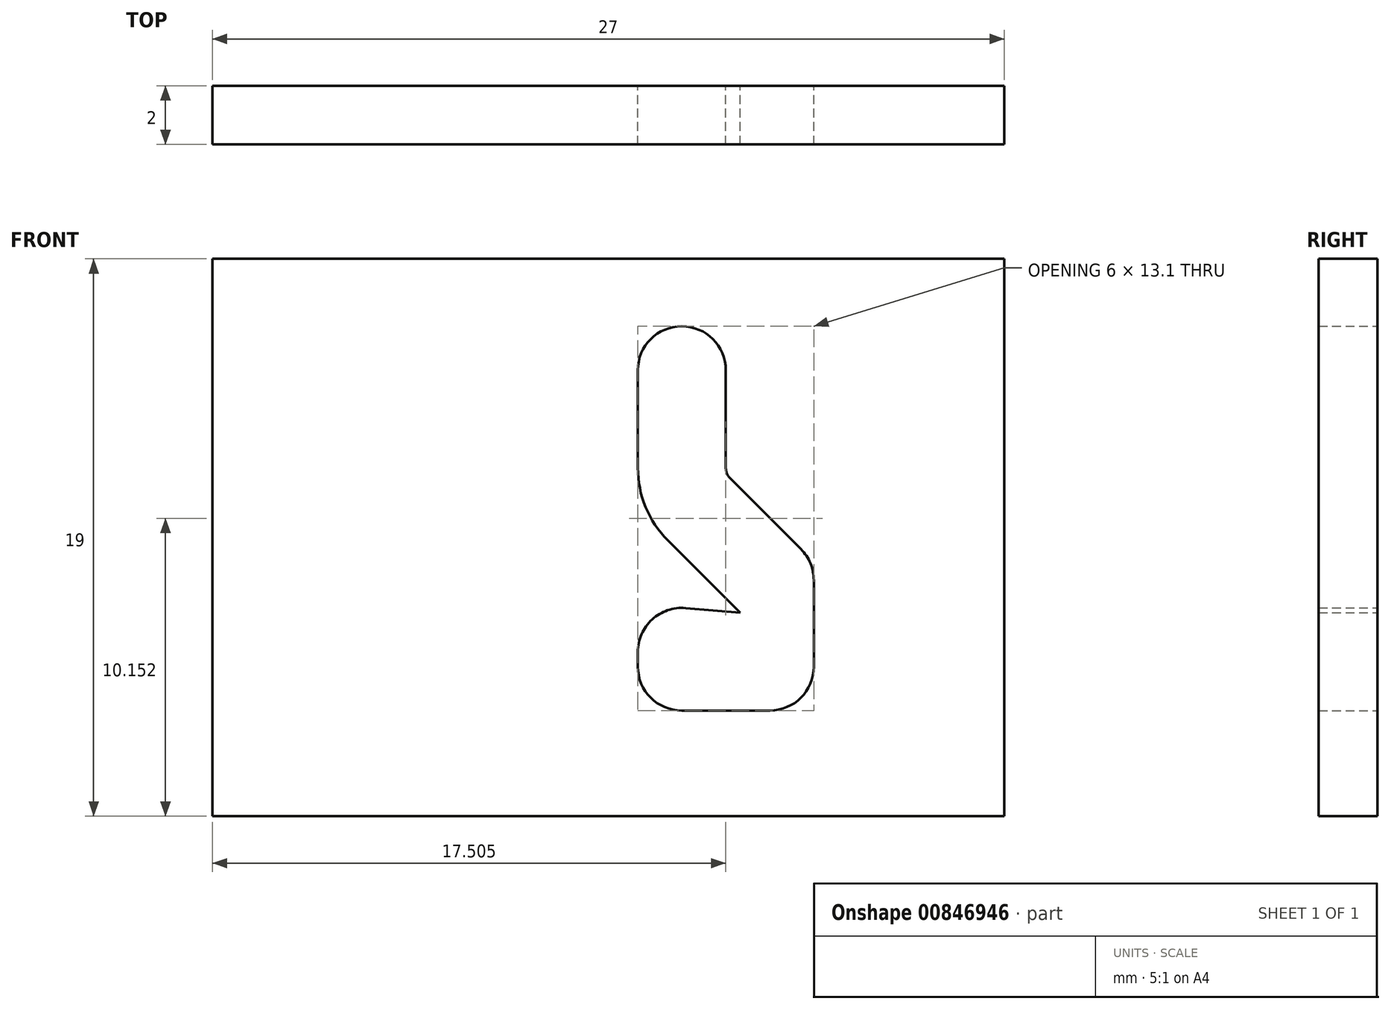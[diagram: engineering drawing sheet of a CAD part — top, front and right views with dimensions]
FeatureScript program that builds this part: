
annotation { "Feature Type Name" : "Feature", "Feature Type Description" : "" }
export const myFeature = defineFeature(function(context is Context, id is Id, definition is map)
    precondition{}
    {
        {
            var Q0;
            Q0=qCreatedBy(makeId("Front.planeOp"),FACE);
            var sketch = newSketch(context, id + "F0", { "sketchPlane" : qUnion([Q0])});
            skCircle(sketch, "E0", {"center": v(-43.9, 12.25) * mm, "radius": 1.5 * mm});
            skCircle(sketch, "E1", {"center": v(-43.9, 2.65) * mm, "radius": 1.5 * mm});
            skLineSegment(sketch, "E2", {"start": v(-43.9, 18) * mm, "end": v(-43.9, 4.16) * mm, "construction": true});
            skLineSegment(sketch, "E3", {"start": v(-49.9, 2.65) * mm, "end": v(-33.42, 2.65) * mm, "construction": true});
            skCircle(sketch, "E4", {"center": v(-40.9, 5.1) * mm, "radius": 1.5 * mm});
            skLineSegment(sketch, "E5", {"start": v(-45.4, 12.25) * mm, "end": v(-45.4, 7.47) * mm});
            skLineSegment(sketch, "E6", {"start": v(-42.4, 12.25) * mm, "end": v(-42.4, 8.72) * mm});
            skLineSegment(sketch, "E7", {"start": v(-42.4, 8.72) * mm, "end": v(-39.83, 6.16) * mm});
            skCircle(sketch, "E8", {"center": v(-43.9, 2.15) * mm, "radius": 1.5 * mm});
            skLineSegment(sketch, "E9", {"start": v(-43.9, 0.65) * mm, "end": v(-40.9, 0.65) * mm});
            skLineSegment(sketch, "E10", {"start": v(-43.9, 4.16) * mm, "end": v(-41.9, 3.98) * mm});
            skLineSegment(sketch, "E11", {"start": v(-45.4, 7.47) * mm, "end": v(-41.9, 3.98) * mm});
            skCircle(sketch, "E12", {"center": v(-40.9, 2.15) * mm, "radius": 1.5 * mm});
            skLineSegment(sketch, "E13", {"start": v(-40.9, 5.1) * mm, "end": v(-40.9, -5.92) * mm, "construction": true});
            skLineSegment(sketch, "E14", {"start": v(-39.4, 5.1) * mm, "end": v(-39.4, 2.15) * mm});
            skLineSegment(sketch, "E15", {"start": v(-45.4, 2.65) * mm, "end": v(-45.4, 2.15) * mm});
            skLineSegment(sketch, "E16.bottom", {"start": v(-59.9, 16.05) * mm, "end": v(-32.9, 16.05) * mm});
            skLineSegment(sketch, "E16.top", {"start": v(-59.9, -2.95) * mm, "end": v(-32.9, -2.95) * mm});
            skLineSegment(sketch, "E16.left", {"start": v(-59.9, 16.05) * mm, "end": v(-59.9, -2.95) * mm});
            skLineSegment(sketch, "E16.right", {"start": v(-32.9, 16.05) * mm, "end": v(-32.9, -2.95) * mm});
            skSolve(sketch);
        }
        {
            var Q0;
            {var subQ9=sQuery(id+"F0.wireOp",EDGE,"E5");Q0=makeQuery(id+"F0.imprint","IMPRINT",FACE,{"disambiguationData":[TD([[makeQuery(id+"F0.imprint","IMPRINT",EDGE,{"derivedFrom":subQ9}),-1.0]])]});}
            extrude(context, id + "F1", {"entities" : qUnion([Q0]), "depth" : 2 * mm, "offsetDistance" : 25 * mm});
        }
        {
            var Q0;
            Q0=makeQuery(id+"F1.opExtrude","SWEPT_EDGE",EDGE,{"disambiguationData":[OSD([sQuery(id+"F0.wireOp",EDGE,"E5"),sQuery(id+"F0.wireOp",EDGE,"E11")])]});
            fillet(context, id + "F2", {"entities" : qUnion([Q0]), "radius" : 3.5 * mm, "tangentPropagation" : true, "allowEdgeOverflow" : false});
        }
        {
            var Q0;
            Q0=makeQuery(id+"F1.opExtrude","SWEPT_EDGE",EDGE,{"disambiguationData":[OSD([sQuery(id+"F0.wireOp",EDGE,"E6"),sQuery(id+"F0.wireOp",EDGE,"E7")])]});
            fillet(context, id + "F3", {"entities" : qUnion([Q0]), "radius" : 0.5 * mm, "tangentPropagation" : true, "allowEdgeOverflow" : false});
        }
    });
